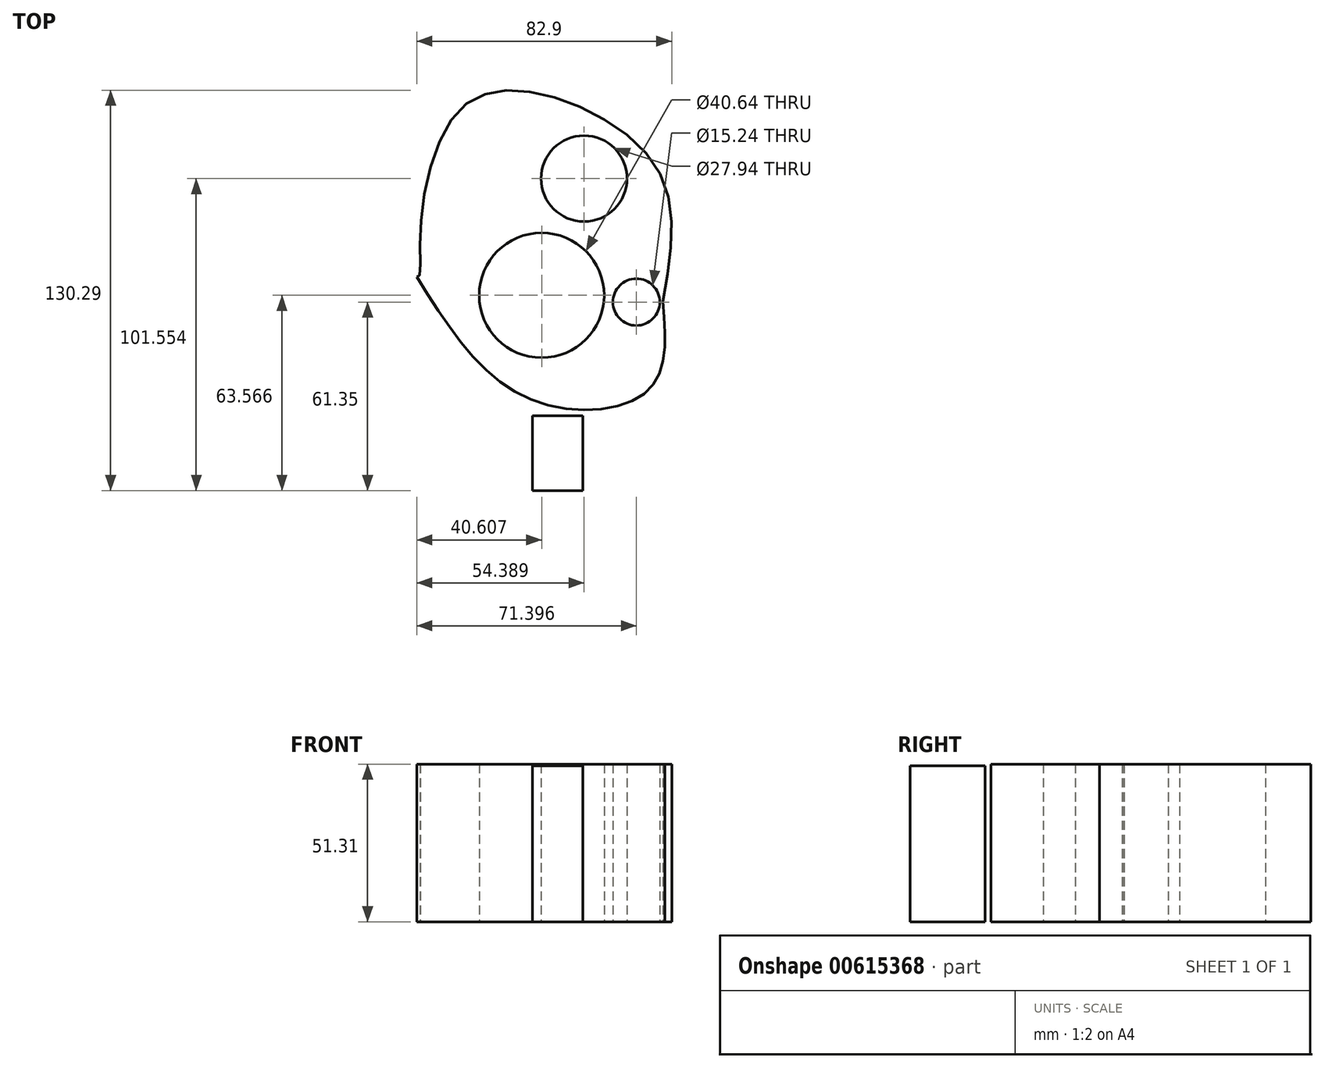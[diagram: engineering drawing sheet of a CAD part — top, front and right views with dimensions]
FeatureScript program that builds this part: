
annotation { "Feature Type Name" : "Feature", "Feature Type Description" : "" }
export const myFeature = defineFeature(function(context is Context, id is Id, definition is map)
    precondition{}
    {
        {
            var Q0;
            Q0=qCreatedBy(makeId("Top.planeOp"),FACE);
            var sketch = newSketch(context, id + "F0", { "sketchPlane" : qUnion([Q0])});
            skFitSpline(sketch, "E0", {"points": [v(56.01, -7.96) * mm, v(55.26, 33.34) * mm, v(20.32, 58.53) * mm, v(-9.33, 55.12) * mm, v(-22.74, 16.46) * mm, v(-23.36, 0) * mm, v(-24.02, 0) * mm], "startDerivative": vector(36.1, 204.47) * mm, "endDerivative": vector(-26.56, 9.14) * mm});
            skFitSpline(sketch, "E1", {"points": [v(56.01, -7.96) * mm, v(51.37, -36.71) * mm, v(12.56, -39.63) * mm, v(-24.02, 0) * mm], "startDerivative": vector(10.16, -117.6) * mm, "endDerivative": vector(-79.9, 127.33) * mm});
            skSolve(sketch);
        }
        {
            var Q0;
            Q0=makeQuery(id+"F0.imprint","IMPRINT",FACE,{"disambiguationData":[TD([[makeQuery(id+"F0.imprint","IMPRINT",EDGE,{"derivedFrom":sQuery(id+"F0.wireOp",EDGE,"E0")}),1.0]])]});
            extrude(context, id + "F1", {"entities" : qUnion([Q0]), "depth" : 51.3 * mm, "offsetDistance" : 25.4 * mm});
        }
        {
            var Q0;
            Q0=qCreatedBy(makeId("Top.planeOp"),FACE);
            var sketch = newSketch(context, id + "F2", { "sketchPlane" : qUnion([Q0])});
            skCircle(sketch, "E2", {"center": v(38.82, -12.65) * mm, "radius": 8.72 * mm});
            skCircle(sketch, "E3", {"center": v(36.21, -4.33) * mm, "radius": 2.27 * mm});
            skCircle(sketch, "E4", {"center": v(16.59, -5.96) * mm, "radius": 19.6 * mm});
            skSolve(sketch);
        }
        {
            var Q0;
            Q0=sQuery(id+"F2.wireOp",VERTEX,"E4.center");
            var Q1;
            Q1=makeQuery(id+"F1.opExtrude","SWEPT_BODY",BODY,{"disambiguationData":[OSD([sQuery(id+"F0.wireOp",EDGE,"E0"),sQuery(id+"F0.wireOp",EDGE,"E1")])]});
            hole(context, id + "F3", {"style" : HoleStyle.SIMPLE, "endStyle" : HoleEndStyle.THROUGH, "oppositeDirection" : true, "holeDiameter" : 40.64 * mm, "majorDiameter" : 6.35 * mm, "isTappedThrough" : true, "tappedDepth" : 12.7 * mm, "tapClearance" : 3, "locations" : qUnion([Q0]), "scope" : qUnion([Q1])});
        }
        {
            var Q0;
            Q0=qCreatedBy(makeId("Top.planeOp"),FACE);
            var sketch = newSketch(context, id + "F4", { "sketchPlane" : qUnion([Q0])});
            skCircle(sketch, "E5", {"center": v(47.38, -8.18) * mm, "radius": 6.93 * mm});
            skSolve(sketch);
        }
        {
            var Q0;
            Q0=sQuery(id+"F4.wireOp",VERTEX,"E5.center");
            var Q1;
            Q1=makeQuery(id+"F1.opExtrude","SWEPT_BODY",BODY,{"disambiguationData":[OSD([sQuery(id+"F0.wireOp",EDGE,"E0"),sQuery(id+"F0.wireOp",EDGE,"E1")])]});
            hole(context, id + "F5", {"style" : HoleStyle.SIMPLE, "endStyle" : HoleEndStyle.THROUGH, "oppositeDirection" : true, "holeDiameter" : 15.24 * mm, "majorDiameter" : 6.35 * mm, "isTappedThrough" : true, "tappedDepth" : 12.7 * mm, "tapClearance" : 3, "locations" : qUnion([Q0]), "scope" : qUnion([Q1])});
        }
        {
            var Q0;
            Q0=qCreatedBy(makeId("Top.planeOp"),FACE);
            var sketch = newSketch(context, id + "F6", { "sketchPlane" : qUnion([Q0])});
            skCircle(sketch, "E6", {"center": v(30.37, 32.02) * mm, "radius": 16.62 * mm});
            skSolve(sketch);
        }
        {
            var Q0;
            Q0=sQuery(id+"F6.wireOp",VERTEX,"E6.center");
            var Q1;
            Q1=makeQuery(id+"F1.opExtrude","SWEPT_BODY",BODY,{"disambiguationData":[OSD([sQuery(id+"F0.wireOp",EDGE,"E0"),sQuery(id+"F0.wireOp",EDGE,"E1")])]});
            hole(context, id + "F7", {"style" : HoleStyle.SIMPLE, "endStyle" : HoleEndStyle.THROUGH, "oppositeDirection" : true, "holeDiameter" : 27.94 * mm, "majorDiameter" : 6.35 * mm, "isTappedThrough" : true, "tappedDepth" : 12.7 * mm, "tapClearance" : 3, "locations" : qUnion([Q0]), "scope" : qUnion([Q1])});
        }
        {
            var Q0;
            Q0=qCreatedBy(makeId("Top.planeOp"),FACE);
            var sketch = newSketch(context, id + "F8", { "sketchPlane" : qUnion([Q0])});
            skLineSegment(sketch, "E7", {"start": v(41.52, -45.2) * mm, "end": v(18.31, -45.2) * mm});
            skLineSegment(sketch, "E8", {"start": v(29.92, -45.2) * mm, "end": v(29.92, -69.53) * mm});
            skLineSegment(sketch, "E9", {"start": v(29.92, -69.53) * mm, "end": v(13.59, -69.53) * mm});
            skLineSegment(sketch, "E10", {"start": v(13.59, -69.53) * mm, "end": v(13.59, -45.2) * mm});
            skLineSegment(sketch, "E11", {"start": v(13.59, -45.2) * mm, "end": v(18.31, -45.2) * mm});
            skLineSegment(sketch, "E12", {"start": v(13.59, -45.2) * mm, "end": v(0, -45.2) * mm});
            skSolve(sketch);
        }
        {
            var Q0;
            {var subQ0=sQuery(id+"F8.wireOp",EDGE,"E8");Q0=makeQuery(id+"F8.imprint","IMPRINT",FACE,{"disambiguationData":[TD([[makeQuery(id+"F8.imprint","IMPRINT",EDGE,{"derivedFrom":subQ0}),-1.0]])]});}
            extrude(context, id + "F9", {"entities" : qUnion([Q0]), "depth" : 50.8 * mm, "offsetDistance" : 25.4 * mm});
        }
    });
